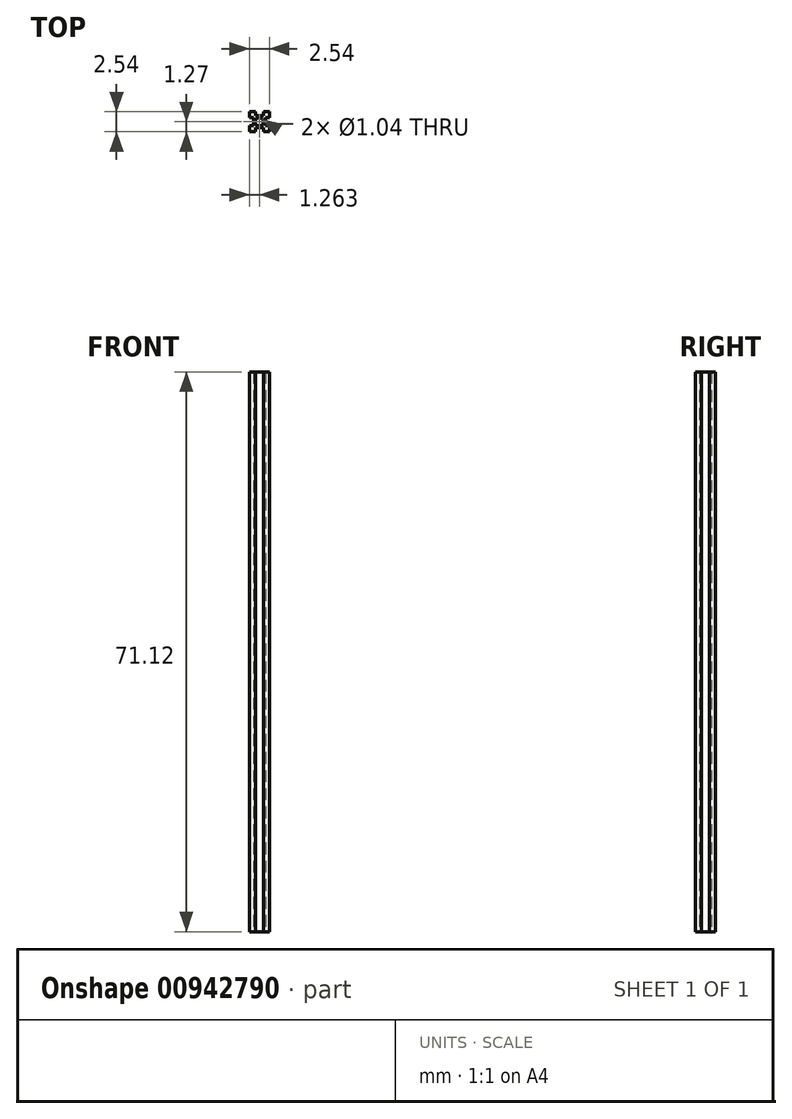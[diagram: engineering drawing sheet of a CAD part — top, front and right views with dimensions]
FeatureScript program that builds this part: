
annotation { "Feature Type Name" : "Feature", "Feature Type Description" : "" }
export const myFeature = defineFeature(function(context is Context, id is Id, definition is map)
    precondition{}
    {
        {
            var Q0;
            Q0=qCreatedBy(makeId("Top.planeOp"),FACE);
            var sketch = newSketch(context, id + "F0", { "sketchPlane" : qUnion([Q0])});
            skLineSegment(sketch, "E0.bottom", {"start": v(0, 0) * mm, "end": v(2.54, 0) * mm});
            skLineSegment(sketch, "E0.top", {"start": v(0, 2.54) * mm, "end": v(2.54, 2.54) * mm});
            skLineSegment(sketch, "E0.left", {"start": v(0, 0) * mm, "end": v(0, 2.54) * mm});
            skLineSegment(sketch, "E0.right", {"start": v(2.54, 0) * mm, "end": v(2.54, 2.54) * mm});
            skLineSegment(sketch, "E1", {"start": v(0, 1.27) * mm, "end": v(1.26, 1.27) * mm});
            skCircle(sketch, "E2", {"center": v(1.26, 1.27) * mm, "radius": 0.52 * mm});
            skLineSegment(sketch, "E3.bottom", {"start": v(0.76, 2.54) * mm, "end": v(1.78, 2.54) * mm});
            skLineSegment(sketch, "E3.top", {"start": v(0.76, 2.04) * mm, "end": v(1.78, 2.04) * mm});
            skLineSegment(sketch, "E3.left", {"start": v(0.76, 2.54) * mm, "end": v(0.76, 2.04) * mm});
            skLineSegment(sketch, "E3.right", {"start": v(1.78, 2.54) * mm, "end": v(1.78, 2.04) * mm});
            skLineSegment(sketch, "E4.bottom", {"start": v(1.78, 0) * mm, "end": v(0.77, 0) * mm});
            skLineSegment(sketch, "E4.top", {"start": v(1.78, 0.5) * mm, "end": v(0.77, 0.5) * mm});
            skLineSegment(sketch, "E4.left", {"start": v(1.78, 0) * mm, "end": v(1.78, 0.5) * mm});
            skLineSegment(sketch, "E4.right", {"start": v(0.77, 0) * mm, "end": v(0.77, 0.5) * mm});
            skLineSegment(sketch, "E5.bottom", {"start": v(2.54, 0.77) * mm, "end": v(2.03, 0.77) * mm});
            skLineSegment(sketch, "E5.top", {"start": v(2.54, 1.79) * mm, "end": v(2.03, 1.79) * mm});
            skLineSegment(sketch, "E5.left", {"start": v(2.54, 0.77) * mm, "end": v(2.54, 1.79) * mm});
            skLineSegment(sketch, "E5.right", {"start": v(2.03, 0.77) * mm, "end": v(2.03, 1.79) * mm});
            skLineSegment(sketch, "E6.bottom", {"start": v(0, 1.79) * mm, "end": v(0.52, 1.79) * mm});
            skLineSegment(sketch, "E6.top", {"start": v(0, 0.77) * mm, "end": v(0.52, 0.77) * mm});
            skLineSegment(sketch, "E6.left", {"start": v(0, 1.79) * mm, "end": v(0, 0.77) * mm});
            skLineSegment(sketch, "E6.right", {"start": v(0.52, 1.79) * mm, "end": v(0.52, 0.77) * mm});
            skSolve(sketch);
        }
        {
            var Q0;
            Q0=makeQuery(id+"F0.imprint","IMPRINT",FACE,{"disambiguationData":[TD([[makeQuery(id+"F0.imprint","IMPRINT",EDGE,{"derivedFrom":sQuery(id+"F0.wireOp",EDGE,"E2")}),-1.0]])]});
            extrude(context, id + "F1", {"entities" : qUnion([Q0]), "depth" : 71.12 * mm, "offsetDistance" : 25.4 * mm});
        }
    });
